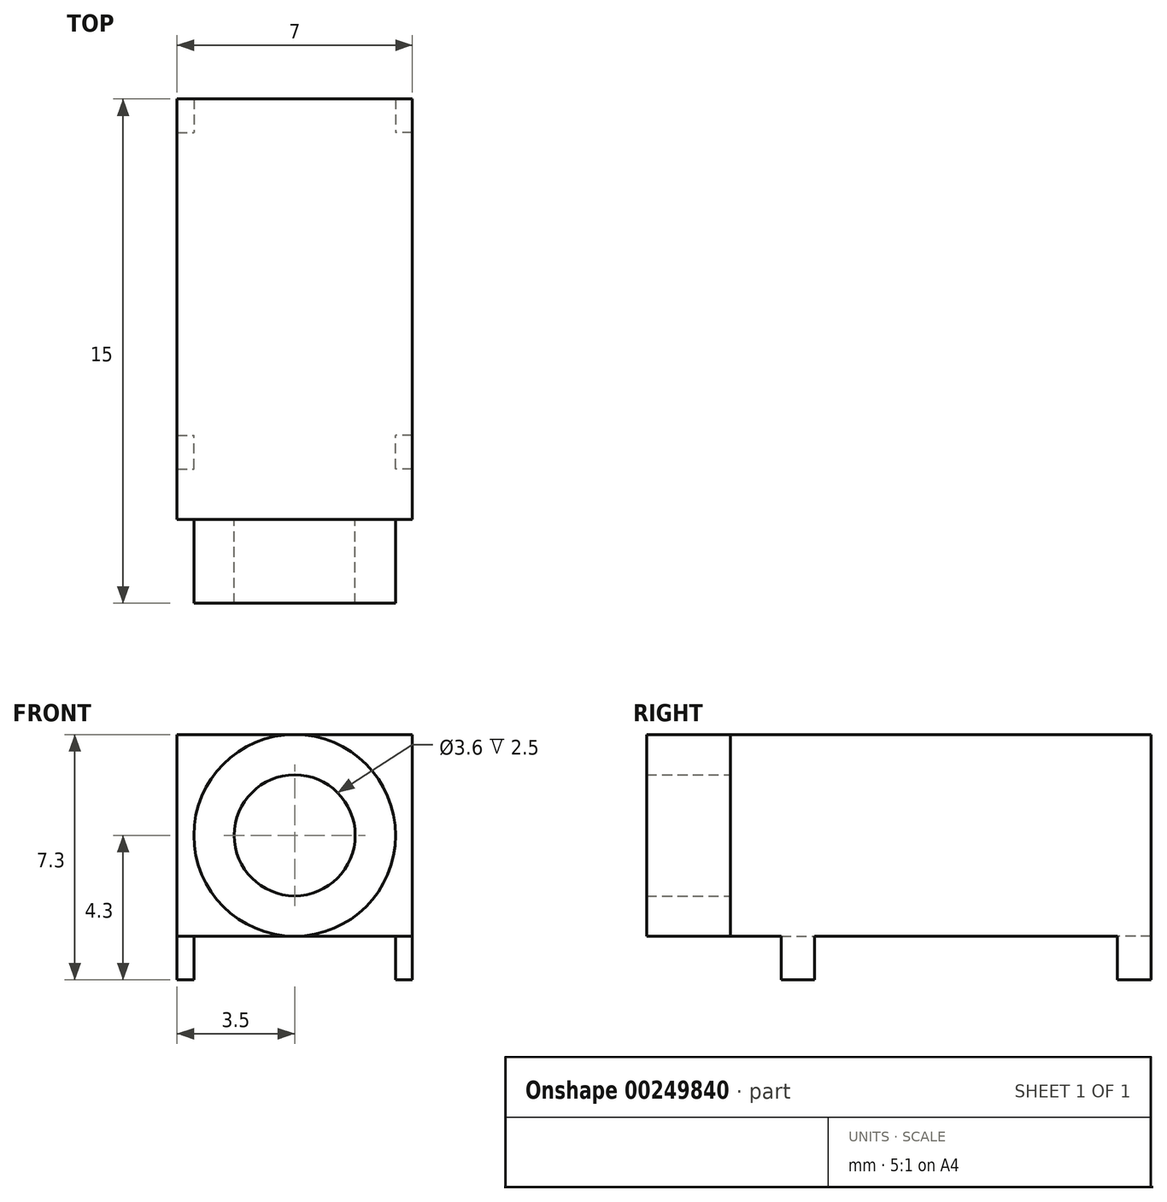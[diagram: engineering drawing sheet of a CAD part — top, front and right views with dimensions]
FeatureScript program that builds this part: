
annotation { "Feature Type Name" : "Feature", "Feature Type Description" : "" }
export const myFeature = defineFeature(function(context is Context, id is Id, definition is map)
    precondition{}
    {
        {
            var Q0;
            Q0=qCreatedBy(makeId("Front.planeOp"),FACE);
            var sketch = newSketch(context, id + "F0", { "sketchPlane" : qUnion([Q0])});
            skLineSegment(sketch, "E0.bottom", {"start": v(0, 0) * mm, "end": v(7, 0) * mm});
            skLineSegment(sketch, "E0.top", {"start": v(0, 6) * mm, "end": v(7, 6) * mm});
            skLineSegment(sketch, "E0.left", {"start": v(0, 0) * mm, "end": v(0, 6) * mm});
            skLineSegment(sketch, "E0.right", {"start": v(7, 0) * mm, "end": v(7, 6) * mm});
            skSolve(sketch);
        }
        {
            var Q0;
            Q0 = qSketchRegion(id + "F0", true);
            extrude(context, id + "F1", {"entities" : qUnion([Q0]), "depth" : 12.5 * mm});
        }
        {
            var Q0;
            Q0=makeQuery(id+"F1.opExtrude","CAP_FACE",FACE,{"disambiguationData":[OSD([sQuery(id+"F0.wireOp",EDGE,"E0.bottom"),sQuery(id+"F0.wireOp",EDGE,"E0.top"),sQuery(id+"F0.wireOp",EDGE,"E0.left"),sQuery(id+"F0.wireOp",EDGE,"E0.right")])],"isStart":false});
            var sketch = newSketch(context, id + "F2", { "sketchPlane" : qUnion([Q0])});
            skCircle(sketch, "E1", {"center": v(3.5, 3) * mm, "radius": 3 * mm});
            skLineSegment(sketch, "E2", {"start": v(3.5, 0) * mm, "end": v(3.5, 6) * mm, "construction": true});
            skCircle(sketch, "E3", {"center": v(3.5, 3) * mm, "radius": 1.8 * mm});
            skSolve(sketch);
        }
        {
            var Q0;
            Q0 = qSketchRegion(id + "F2", true);
            extrude(context, id + "F3", {"entities" : qUnion([Q0]), "operationType" : NewBodyOperationType.ADD, "depth" : 2.5 * mm});
        }
        {
            var Q0;
            Q0=makeQuery(id+"F1.opExtrude","SWEPT_FACE",FACE,{"disambiguationData":[OSD([sQuery(id+"F0.wireOp",EDGE,"E0.bottom")])]});
            var sketch = newSketch(context, id + "F4", { "sketchPlane" : qUnion([Q0])});
            skLineSegment(sketch, "E4", {"start": v(3.5, 12.5) * mm, "end": v(3.5, 0) * mm, "construction": true});
            skLineSegment(sketch, "E5.bottom", {"start": v(0, 0) * mm, "end": v(0.5, 0) * mm});
            skLineSegment(sketch, "E5.top", {"start": v(0, 1) * mm, "end": v(0.5, 1) * mm});
            skLineSegment(sketch, "E5.left", {"start": v(0, 0) * mm, "end": v(0, 1) * mm});
            skLineSegment(sketch, "E5.right", {"start": v(0.5, 0) * mm, "end": v(0.5, 1) * mm});
            skLineSegment(sketch, "E6.bottom", {"start": v(0, 11) * mm, "end": v(0.5, 11) * mm});
            skLineSegment(sketch, "E6.top", {"start": v(0, 10) * mm, "end": v(0.5, 10) * mm});
            skLineSegment(sketch, "E6.left", {"start": v(0, 11) * mm, "end": v(0, 10) * mm});
            skLineSegment(sketch, "E6.right", {"start": v(0.5, 11) * mm, "end": v(0.5, 10) * mm});
            skLineSegment(sketch, "E7.MirrorCS", {"start": v(7, 10) * mm, "end": v(6.5, 10) * mm});
            skLineSegment(sketch, "E8.MirrorCS", {"start": v(7, 11) * mm, "end": v(6.5, 11) * mm});
            skLineSegment(sketch, "E9.MirrorCS", {"start": v(6.5, 0) * mm, "end": v(6.5, 1) * mm});
            skLineSegment(sketch, "E10.MirrorCS", {"start": v(7, 0) * mm, "end": v(7, 1) * mm});
            skLineSegment(sketch, "E11.MirrorCS", {"start": v(7, 1) * mm, "end": v(6.5, 1) * mm});
            skLineSegment(sketch, "E12.MirrorCS", {"start": v(7, 0) * mm, "end": v(6.5, 0) * mm});
            skLineSegment(sketch, "E13.MirrorCS", {"start": v(7, 11) * mm, "end": v(7, 10) * mm});
            skLineSegment(sketch, "E14.MirrorCS", {"start": v(6.5, 11) * mm, "end": v(6.5, 10) * mm});
            skSolve(sketch);
        }
        {
            var Q0;
            Q0 = qSketchRegion(id + "F4", true);
            extrude(context, id + "F5", {"entities" : qUnion([Q0]), "operationType" : NewBodyOperationType.ADD, "depth" : 1.3 * mm});
        }
    });
